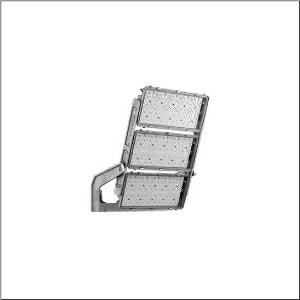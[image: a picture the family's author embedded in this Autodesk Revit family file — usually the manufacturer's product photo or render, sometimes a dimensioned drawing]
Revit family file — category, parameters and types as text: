
# Revit family: floodlight_fl_11_maxi_pro_remote___pl43_5xa779528a01aa_9860
name_source: partatom
category: Lighting Fixtures
units: mm (PartAtom-declared; Revit-internal decimal feet)

## family parameters
Cut with Voids When Loaded = No
Host = Face
Light Source = No
Part Type = Normal
Room Calculation Point = No
Round Connector Dimension = Use Diameter
Shared = No

## types (1)
- --- (1 x LED, 156040 lm, 1388 W, 5700K)
    Apparent Load = 1388 VA
    CIE Flux Codes = 25 74 99 100 100
    Color Rendering = 80
    Color Temperature = 5700K
    Default Elevation = 1800 mm
    Description = Floodlight FL 11  maxi  pro Remote floodlight; light control with lens of PMMA; cover panel of toughened safety glass, transparent; light distribution: PL43, asymmetric direct distribution, LEDcolour temperature: 5700K, rated luminous flux: 156.040lm, colour rendering: CRI > 80, light colour: 857; luminous efficacy: 112lm/W; brightness control: DMX+RDM; with terminal, 8-pole, max. 2.5mm², mains connection: 220..240V/380..400V AC, 50/60Hz, surge voltage resistance: line to ground: 10kV, ECG replaceable separately, LED unit replaceable without ESD environment, dustproof LED module, LED unit replaceable, LED unit replaceable on mast without ESD environment, dimming range 10..100%; 1388W floodlight with 3x LED unit of diecast aluminium, coated grey; length: 1.003mm / width: 651mm / height: 338mm; mounting bracket, of diecast aluminium, uncoated, natural, equipment: Power, protection rating (complete): IP66; insulation class (complete): insulation class I (protective earthing); certification: CE, ENEC, VDE; ball protection: ball impact resistance with accessories, impact resistance: IK07; only for outdoor installations, rated ambient temperature 10°C, permissible operating ambient temperature: -40..+30°C, permissible storage temperature: -40..+85°Cpackaging unit: 1 piece

Light Distribution: PL43
    Height = 320 mm
    Lamp = 1 x LED
    Lamp Light Flux = 156040 lm
    Lamp Power = 1388 W
    Lamp count = 1
    Length = 1002 mm
    Luminous efficacy = 112 lm/W
    Manufacturer = Siteco
    ModVariant = No
    Model = 5XA779528A01AA
    Mounting Place = Ceiling
    Mounting Type = Surface mounted
    Number of Poles = 1
    OnlyDefault = Yes
    Power Factor = 1
    Product Name = Floodlight FL 11 maxi pro Remote | PL43
    Product group = floodlight | ceiling mounted
    ProductGroupID = 301
    Protection Class = Protection class I
    Protection Degree = IP 66
    RLX_Detail_Level = 1
    RLX_Emergency_Light_Flux = 0 lm
    RLX_Emergency_Type = 0
    RLX_Emergency_Type_DB = No
    RlxData = <blob elided: 52369 chars, md5=b6fc0a3c>
    Socket = socket
    Standby Power = 0 W
    System Light Flux = 156040 lm
    System Power = 1388 W
    Type Comments = factory setting: luminous flux: 100 % | dim-lin: 255 | 955 mA
    Type Image = l_1349141.jpg
    URL = http://relux.com
    VarID = @adj_081156
    Voltage = 0 V
    Weight = 0.00 kg
    Width = 655 mm

## geometry (parser evidence)
native form markers: Blend x4, Sweep x13
no freeform markers — native parametric forms only
